FCSTD DOCUMENT  (FreeCAD 1.1R41365 (Git))
Label: FlexureAssembly
License: All rights reserved
LicenseURL: https://en.wikipedia.org/wiki/All_rights_reserved
objects: App::Link×7, App::Point×1, App::FeaturePython×1, Assembly::JointGroup×1, Assembly::AssemblyObject×1
EXTERNAL_REF file=WireMount.FCStd obj=Body
EXTERNAL_REF file=FlexureWire.FCStd obj=Body
EXTERNAL_REF file=FlexureStiffener.FCStd obj=Body
EXTERNAL_REF file=WireMountFixture.FCStd obj=Body

FEATURE [App::Point] Origin001
  Role = Origin
FEATURE [App::Link] WireMount  label="WireMount1"
  LinkedObject = -> <external WireMount.FCStd>#Body
FEATURE [App::FeaturePython] GroundedJoint  # Assembly grounded joint (typed FeaturePython)
  ObjectToGround = -> WireMount
FEATURE [Assembly::JointGroup] Joints
  Group = -> [GroundedJoint]
FEATURE [App::Link] WireMount001  label="WireMount2"
  LinkPlacement = pos=(0,-55,3) rot=(1,0,0;3.14159rad)
  LinkedObject = -> <external WireMount.FCStd>#Body
  Placement = pos=(0,-55,3) rot=(1,0,0;3.14159rad)
FEATURE [App::Link] FlexureWire  label="FlexureWire1"
  LinkPlacement = pos=(8,3.5,1.5) rot=(0,0,1;0rad)
  LinkedObject = -> <external FlexureWire.FCStd>#Body
  Placement = pos=(8,3.5,1.5) rot=(0,0,1;0rad)
FEATURE [App::Link] FlexureWire001  label="FlexureWire2"
  LinkPlacement = pos=(-8.00001,3.5,1.5) rot=(0,0,1;0rad)
  LinkedObject = -> <external FlexureWire.FCStd>#Body
  Placement = pos=(-8.00001,3.5,1.5) rot=(0,0,1;0rad)
FEATURE [App::Link] Rod  label="FlexureStiffener1"
  LinkPlacement = pos=(-8,-27.5,1.5) rot=(0,0,1;0rad)
  LinkedObject = -> <external FlexureStiffener.FCStd>#Body
  Placement = pos=(-8,-27.5,1.5) rot=(0,0,1;0rad)
FEATURE [App::Link] FlexureStiffener  label="FlexureStiffener2"
  LinkPlacement = pos=(8,-27.5,1.5) rot=(0,0,1;0rad)
  LinkedObject = -> <external FlexureStiffener.FCStd>#Body
  Placement = pos=(8,-27.5,1.5) rot=(0,0,1;0rad)
FEATURE [App::Link] WireMountFixture
  LinkPlacement = pos=(0,-27.5,-5) rot=(0,0,1;0rad)
  LinkedObject = -> <external WireMountFixture.FCStd>#Body
  Placement = pos=(0,-27.5,-5) rot=(0,0,1;0rad)
FEATURE [Assembly::AssemblyObject] Assembly  label="FlexureAssembly"
  Group = -> [Joints,WireMount,GroundedJoint,WireMount001,FlexureWire,FlexureWire001,Rod,FlexureStiffener,WireMountFixture]
  Origin = -> Origin
  Type = Assembly

RESOLVED EXTERNAL PARTS (link-assembly join: the EXTERNAL_REF files above that resolve inside this repo's crawl, each included once):
---- part FlexureStiffener.FCStd = doc fcstd_d9e3d32cc4ef ----
FCSTD DOCUMENT  (FreeCAD 1.1R41365 (Git))
Label: FlexureStiffener
License: All rights reserved
LicenseURL: https://en.wikipedia.org/wiki/All_rights_reserved
objects: App::Point×1, Sketcher::SketchObject×1, PartDesign::Pad×1, PartDesign::Fillet×1, PartDesign::Body×1
note: 9 computed .brp shape members not serialized (recipe doc carries the construction recipe); baked Part::Feature solids carry a one-line shape summary decoded from their .brp

FEATURE [App::Point] Origin001
  Role = Origin
FEATURE [Sketcher::SketchObject] Sketch
  ArcFitTolerance = 1e-06
  AttachmentSupport = -> [XZ_Plane]
  ExternalTypes = [0]
  FullyConstrained = true
  MakeInternals = false
  MapMode = 5
  Placement = pos=(0,0,0) rot=(1,0,0;1.5708rad)
  sketch-geometry (14):
    g0: LineSegment StartX=0.669696 StartY=1.61679 StartZ=0 EndX=-0.669696 EndY=1.61679 EndZ=0
    g1: LineSegment StartX=-0.669696 StartY=1.61679 StartZ=0 EndX=-1.61679 EndY=0.669696 EndZ=0
    g2: LineSegment StartX=-1.61679 StartY=0.669696 StartZ=0 EndX=-1.61679 EndY=-0.669696 EndZ=0
    g3: LineSegment StartX=-1.61679 StartY=-0.669696 StartZ=0 EndX=-0.669696 EndY=-1.61679 EndZ=0
    g4: LineSegment StartX=-0.669696 StartY=-1.61679 StartZ=0 EndX=0.669696 EndY=-1.61679 EndZ=0
    g5: LineSegment StartX=0.669696 StartY=-1.61679 StartZ=0 EndX=1.61679 EndY=-0.669696 EndZ=0
    g6: LineSegment StartX=1.61679 StartY=-0.669696 StartZ=0 EndX=1.61679 EndY=0.669696 EndZ=0
    g7: LineSegment StartX=1.61679 StartY=0.669696 StartZ=0 EndX=0.669696 EndY=1.61679 EndZ=0
    g8: Circle [constr] CenterX=0 CenterY=0 CenterZ=0 NormalX=0 NormalY=0 NormalZ=1 AngleXU=0 Radius=1.75
    g9: LineSegment StartX=-0.3 StartY=-0.325 StartZ=0 EndX=0.3 EndY=-0.325 EndZ=0
    g10: LineSegment StartX=0.3 StartY=-0.325 StartZ=0 EndX=0.3 EndY=0.325 EndZ=0
    g11: LineSegment StartX=0.3 StartY=0.325 StartZ=0 EndX=-0.3 EndY=0.325 EndZ=0
    g12: LineSegment StartX=-0.3 StartY=0.325 StartZ=0 EndX=-0.3 EndY=-0.325 EndZ=0
    g13: GeomPoint [constr] X=0 Y=0 Z=0
  constraints (32):
    c: Coincident(g0,g1)
    c: Coincident(g1,g2)
    c: Coincident(g2,g3)
    c: Coincident(g3,g4)
    c: Coincident(g4,g5)
    c: Coincident(g5,g6)
    c: Coincident(g6,g7)
    c: Coincident(g7,g0)
    c: Equal(g0, g1-g7) x7
    c: PointOnObject(g0,g8)
    c: PointOnObject(g1,g8)
    c: PointOnObject(g2,g8)
    c: PointOnObject(g3,g8)
    c: PointOnObject(g4,g8)
    c: PointOnObject(g5,g8)
    c: PointOnObject(g6,g8)
    c: PointOnObject(g7,g8)
    c: Coincident(g8,g-1)
    c: Vertical(g6)
    c: Diameter(g8) = 3.5
    c: Coincident(g9,g10)
    c: Coincident(g10,g11)
    c: Coincident(g11,g12)
    c: Coincident(g12,g9)
    c: Horizontal(g9)
    c: Horizontal(g11)
    c: Vertical(g10)
    c: Vertical(g12)
    c: Symmetric(g11,g9,g13)
    c: Coincident(g13,g8)
    c: DistanceY(g10,g10) = 0.65
    c: DistanceX(g11,g11) = 0.6
FEATURE [PartDesign::Pad] Pad
  Direction = (0,-1,2e-16)
  Length = 40
  Length2 = 10
  Midplane = true
  Placement = pos=(0,0,0) rot=(1,0,0;1.5708rad)
  Profile = -> Sketch
  ReferenceAxis = -> Sketch [N_Axis]
  Refine = true
  Suppressed = false
  Type = 0
FEATURE [PartDesign::Fillet] Fillet
  Base = -> Pad [Edge5,Edge8,Edge20,Edge17]
  BaseFeature = -> Pad
  Placement = pos=(0,0,0) rot=(1,0,0;1.5708rad)
  Radius = 0.25
  Refine = true
  SupportTransform = false
  Suppressed = false
  UseAllEdges = false
FEATURE [PartDesign::Body] Body  label="FlexureStiffener"
  AllowCompound = false
  Group = -> [Sketch,Pad,Fillet]
  Origin = -> Origin
  Tip = -> Fillet
---- part FlexureWire.FCStd = doc fcstd_ac3010708b95 ----
FCSTD DOCUMENT  (FreeCAD 1.1R41365 (Git))
Label: FlexureWire
License: All rights reserved
LicenseURL: https://en.wikipedia.org/wiki/All_rights_reserved
objects: App::Point×1, Sketcher::SketchObject×1, PartDesign::Pad×1, PartDesign::Body×1
note: 6 computed .brp shape members not serialized (recipe doc carries the construction recipe); baked Part::Feature solids carry a one-line shape summary decoded from their .brp

FEATURE [App::Point] Origin001
  Role = Origin
FEATURE [Sketcher::SketchObject] Sketch
  ArcFitTolerance = 1e-06
  AttachmentSupport = -> [XZ_Plane]
  ExternalTypes = [0]
  FullyConstrained = true
  MakeInternals = false
  MapMode = 5
  Placement = pos=(0,0,0) rot=(1,0,0;1.5708rad)
  sketch-geometry (1):
    g0: Circle CenterX=0 CenterY=0 CenterZ=0 NormalX=0 NormalY=0 NormalZ=1 AngleXU=0 Radius=0.25
  constraints (2):
    c: Coincident(g0,g-1)
    c: Diameter(g0) = 0.5
FEATURE [PartDesign::Pad] Pad
  Direction = (0,-1,0)
  Length = 62
  Length2 = 10
  Placement = pos=(0,0,0) rot=(1,0,0;1.5708rad)
  Profile = -> Sketch
  ReferenceAxis = -> Sketch [N_Axis]
  Refine = true
  Suppressed = false
  Type = 0
FEATURE [PartDesign::Body] Body  label="FlexureWire"
  AllowCompound = false
  Group = -> [Sketch,Pad]
  Origin = -> Origin
  Tip = -> Pad
---- part WireMount.FCStd = doc fcstd_70210a3bc8ae ----
FCSTD DOCUMENT  (FreeCAD 1.1R41365 (Git))
Label: WireMount
License: All rights reserved
LicenseURL: https://en.wikipedia.org/wiki/All_rights_reserved
objects: Sketcher::SketchObject×3, PartDesign::Pocket×2, PartDesign::Chamfer×2, App::Point×1, PartDesign::Pad×1, PartDesign::Fillet×1, PartDesign::Mirrored×1, PartDesign::Body×1
note: 27 computed .brp shape members not serialized (recipe doc carries the construction recipe); baked Part::Feature solids carry a one-line shape summary decoded from their .brp

FEATURE [App::Point] Origin001
  Role = Origin
FEATURE [Sketcher::SketchObject] Sketch
  ArcFitTolerance = 1e-06
  AttachmentSupport = -> [XY_Plane]
  ExternalTypes = [0]
  FullyConstrained = true
  MakeInternals = false
  MapMode = 5
  sketch-geometry (5):
    g0: LineSegment StartX=-10 StartY=-2.75 StartZ=0 EndX=0 EndY=-2.75 EndZ=0
    g1: LineSegment StartX=0 StartY=-2.75 StartZ=0 EndX=0 EndY=2.75 EndZ=0
    g2: LineSegment StartX=0 StartY=2.75 StartZ=0 EndX=-10 EndY=2.75 EndZ=0
    g3: LineSegment StartX=-10 StartY=2.75 StartZ=0 EndX=-10 EndY=-2.75 EndZ=0
    g4: GeomPoint [constr] X=0 Y=0 Z=0
  constraints (12):
    c: Coincident(g0,g1)
    c: Coincident(g1,g2)
    c: Coincident(g2,g3)
    c: Coincident(g3,g0)
    c: Horizontal(g0)
    c: Horizontal(g2)
    c: Vertical(g1)
    c: Vertical(g3)
    c: Coincident(g4,g-1)
    c: DistanceX(g0,g0) = 10
    c: DistanceY(g1,g1) = 5.5
    c: Symmetric(g1,g1,g4)
FEATURE [PartDesign::Pad] Pad
  Direction = (0,0,1)
  Length = 3
  Length2 = 10
  Profile = -> Sketch
  ReferenceAxis = -> Sketch [N_Axis]
  Refine = true
  Suppressed = false
  Type = 0
FEATURE [Sketcher::SketchObject] Sketch001
  ArcFitTolerance = 1e-06
  AttachmentSupport = -> [Pad]
  ExternalTypes = [0]
  FullyConstrained = true
  MakeInternals = false
  MapMode = 5
  Placement = pos=(0,0,3) rot=(0,0,1;0rad)
  sketch-geometry (1):
    g0: Circle CenterX=-6 CenterY=0 CenterZ=0 NormalX=0 NormalY=0 NormalZ=1 AngleXU=0 Radius=1.1
  constraints (3):
    c: Diameter(g0) = 2.2
    c: DistanceX(g0,g-1) = 6
    c: PointOnObject(g0,g-1)
FEATURE [PartDesign::Pocket] Pocket
  BaseFeature = -> Pad
  Direction = (0,0,-1)
  Length = 5
  Length2 = 5
  Profile = -> Sketch001
  ReferenceAxis = -> Sketch001 [N_Axis]
  Refine = true
  Suppressed = false
  Type = 1
FEATURE [Sketcher::SketchObject] Sketch002
  ArcFitTolerance = 1e-06
  AttachmentSupport = -> [Pocket]
  ExternalTypes = [0]
  FullyConstrained = true
  MakeInternals = false
  MapMode = 5
  Placement = pos=(0,-2.75,0) rot=(1,0,0;1.5708rad)
  sketch-geometry (5):
    g0: LineSegment StartX=-8.3 StartY=1.2 StartZ=0 EndX=-7.7 EndY=1.2 EndZ=0
    g1: LineSegment StartX=-7.7 StartY=1.2 StartZ=0 EndX=-7.7 EndY=1.8 EndZ=0
    g2: LineSegment StartX=-7.7 StartY=1.8 StartZ=0 EndX=-8.3 EndY=1.8 EndZ=0
    g3: LineSegment StartX=-8.3 StartY=1.8 StartZ=0 EndX=-8.3 EndY=1.2 EndZ=0
    g4: GeomPoint [constr] X=-8 Y=1.5 Z=0
  constraints (13):
    c: Coincident(g0,g1)
    c: Coincident(g1,g2)
    c: Coincident(g2,g3)
    c: Coincident(g3,g0)
    c: Horizontal(g0)
    c: Horizontal(g2)
    c: Vertical(g1)
    c: Vertical(g3)
    c: Symmetric(g2,g0,g4)
    c: DistanceY(g3,g3) = 0.6
    c: DistanceX(g0,g0) = 0.6
    c: DistanceY(g-1,g4) = 1.5
    c: DistanceX(g4,g-1) = 8
FEATURE [PartDesign::Pocket] Pocket001
  BaseFeature = -> Pocket
  Direction = (0,1,-2e-16)
  Length = 5
  Length2 = 5
  Profile = -> Sketch002
  ReferenceAxis = -> Sketch002 [N_Axis]
  Refine = true
  Suppressed = false
  Type = 1
FEATURE [PartDesign::Fillet] Fillet
  Base = -> Pocket001 [Edge1,Edge9]
  BaseFeature = -> Pocket001
  Radius = 0.75
  Refine = true
  SupportTransform = false
  Suppressed = false
  UseAllEdges = false
FEATURE [PartDesign::Mirrored] Mirrored
  BaseFeature = -> Fillet
  MirrorPlane = -> YZ_Plane
  Refine = true
  Suppressed = false
  TransformMode = 1
FEATURE [PartDesign::Chamfer] Chamfer
  Angle = 45
  Base = -> Mirrored [Edge50,Edge52]
  BaseFeature = -> Mirrored
  ChamferType = 0
  FlipDirection = false
  Refine = true
  Size = 1.2
  Size2 = 1
  SupportTransform = false
  Suppressed = false
  UseAllEdges = false
FEATURE [PartDesign::Chamfer] Chamfer001
  Angle = 45
  Base = -> Chamfer [Edge6]
  BaseFeature = -> Chamfer
  ChamferType = 0
  FlipDirection = false
  Refine = true
  Size = 0.4
  Size2 = 1
  SupportTransform = false
  Suppressed = false
  UseAllEdges = false
FEATURE [PartDesign::Body] Body  label="WireMount"
  AllowCompound = false
  Group = -> [Sketch,Pad,Sketch001,Pocket,Sketch002,Pocket001,Fillet,Mirrored,Chamfer,Chamfer001]
  Origin = -> Origin
  Tip = -> Chamfer001
---- part WireMountFixture.FCStd = doc fcstd_843f589c6978 ----
FCSTD DOCUMENT  (FreeCAD 1.1R41365 (Git))
Label: WireMountFixture
License: All rights reserved
LicenseURL: https://en.wikipedia.org/wiki/All_rights_reserved
objects: Sketcher::SketchObject×7, PartDesign::Pocket×6, PartDesign::Fillet×2, PartDesign::Chamfer×2, App::Point×1, PartDesign::Pad×1, Spreadsheet::Sheet×1, PartDesign::Mirrored×1, PartDesign::Body×1
note: 50 computed .brp shape members not serialized (recipe doc carries the construction recipe); baked Part::Feature solids carry a one-line shape summary decoded from their .brp

FEATURE [App::Point] Origin001
  Role = Origin
FEATURE [Sketcher::SketchObject] Sketch
  ArcFitTolerance = 1e-06
  AttachmentSupport = -> [XY_Plane]
  ExternalTypes = [0]
  FullyConstrained = true
  MakeInternals = false
  MapMode = 5
  sketch-geometry (5):
    g0: LineSegment StartX=-12.5 StartY=35 StartZ=0 EndX=-12.5 EndY=0 EndZ=0
    g1: LineSegment StartX=-12.5 StartY=0 StartZ=0 EndX=12.5 EndY=0 EndZ=0
    g2: LineSegment StartX=12.5 StartY=0 StartZ=0 EndX=12.5 EndY=35 EndZ=0
    g3: LineSegment StartX=12.5 StartY=35 StartZ=0 EndX=-12.5 EndY=35 EndZ=0
    g4: GeomPoint [constr] X=0 Y=0 Z=0
  constraints (12):
    c: Coincident(g0,g1)
    c: Coincident(g1,g2)
    c: Coincident(g2,g3)
    c: Coincident(g3,g0)
    c: Vertical(g0)
    c: Vertical(g2)
    c: Horizontal(g1)
    c: Horizontal(g3)
    c: Coincident(g4,g-1)
    c: DistanceX(g3,g3) = 25
    c: Symmetric(g1,g1,g4)
    c: DistanceY(g2,g2) = 35
FEATURE [PartDesign::Pad] Pad
  Direction = (0,0,1)
  Length = 6
  Length2 = 10
  Profile = -> Sketch
  ReferenceAxis = -> Sketch [N_Axis]
  Refine = true
  Suppressed = false
  Type = 0
FEATURE [Sketcher::SketchObject] Sketch002
  ArcFitTolerance = 1e-06
  AttachmentSupport = -> [Pad]
  ExternalTypes = [0]
  FullyConstrained = true
  MakeInternals = false
  MapMode = 5
  Placement = pos=(0,0,6) rot=(0,0,1;0rad)
  sketch-geometry (5):
    g0: LineSegment StartX=10.05 StartY=24.7 StartZ=0 EndX=-10.05 EndY=24.7 EndZ=0
    g1: LineSegment StartX=-10.05 StartY=24.7 StartZ=0 EndX=-10.05 EndY=30.3 EndZ=0
    g2: LineSegment StartX=-10.05 StartY=30.3 StartZ=0 EndX=10.05 EndY=30.3 EndZ=0
    g3: LineSegment StartX=10.05 StartY=30.3 StartZ=0 EndX=10.05 EndY=24.7 EndZ=0
    g4: GeomPoint [constr] X=0 Y=27.5 Z=0
  constraints (13):
    c: Coincident(g0,g1)
    c: Coincident(g1,g2)
    c: Coincident(g2,g3)
    c: Coincident(g3,g0)
    c: Horizontal(g0)
    c: Horizontal(g2)
    c: Vertical(g1)
    c: Vertical(g3)
    c: Symmetric(g2,g0,g4)
    c: PointOnObject(g4,g-2)
    c: DistanceY(g1,g1) = 5.6
    c: Distance(g0,g0) = 20.1
    c: DistanceY(g-1,g4) = 27.5
FEATURE [Spreadsheet::Sheet] Spreadsheet  label="Parameters"
  cells = A1='Cabel Length; B1(CableLength)==75 mm
FEATURE [PartDesign::Pocket] Pocket
  BaseFeature = -> Pad
  Direction = (0,0,-1)
  Length = 1.5
  Length2 = 5
  Profile = -> Sketch002
  ReferenceAxis = -> Sketch002 [N_Axis]
  Refine = true
  Suppressed = false
  Type = 0
FEATURE [Sketcher::SketchObject] Sketch004
  ArcFitTolerance = 1e-06
  AttachmentSupport = -> [Pocket]
  ExternalGeometry = -> [Pocket]
  ExternalTypes = [0,0,0,0]
  FullyConstrained = true
  MakeInternals = false
  MapMode = 5
  Placement = pos=(0,0,6) rot=(0,0,1;0rad)
  sketch-geometry (4):
    g0: Circle CenterX=-10.05 CenterY=30.3 CenterZ=0 NormalX=0 NormalY=0 NormalZ=1 AngleXU=0 Radius=1
    g1: Circle CenterX=10.05 CenterY=30.3 CenterZ=0 NormalX=0 NormalY=0 NormalZ=1 AngleXU=0 Radius=1
    g2: Circle CenterX=-10.05 CenterY=24.7 CenterZ=0 NormalX=0 NormalY=0 NormalZ=1 AngleXU=0 Radius=1
    g3: Circle CenterX=10.05 CenterY=24.7 CenterZ=0 NormalX=0 NormalY=0 NormalZ=1 AngleXU=0 Radius=1
  constraints (9):
    c: Equal(g1,g0)
    c: Diameter(g0) = 2
    c: Horizontal(g1,g0)
    c: Vertical(g-4,g1)
    c: Coincident(g0,g-3)
    c: Coincident(g2,g-6)
    c: Coincident(g3,g-5)
    c: Equal(g2,g0)
    c: Equal(g0,g3)
FEATURE [PartDesign::Pocket] Pocket002
  BaseFeature = -> Pocket
  Direction = (0,0,-1)
  Length = 2
  Length2 = 5
  Profile = -> Sketch004
  ReferenceAxis = -> Sketch004 [N_Axis]
  Refine = true
  Suppressed = false
  Type = 0
FEATURE [Sketcher::SketchObject] Sketch006
  ArcFitTolerance = 1e-06
  AttachmentSupport = -> [Pocket002]
  ExternalTypes = [0]
  FullyConstrained = true
  MakeInternals = false
  MapMode = 5
  Placement = pos=(0,0,6) rot=(0,0,1;0rad)
  sketch-geometry (1):
    g0: Circle CenterX=0 CenterY=27.5 CenterZ=0 NormalX=0 NormalY=0 NormalZ=1 AngleXU=0 Radius=1.5
  constraints (3):
    c: PointOnObject(g0,g-2)
    c: Diameter(g0) = 3
    c: DistanceY(g-1,g0) = 27.5
FEATURE [PartDesign::Fillet] Fillet001
  Base = -> Pocket002 [Edge25,Edge23,Edge29,Edge30,Edge42,Edge41,Edge35]
  BaseFeature = -> Pocket002
  Radius = 0.5
  Refine = true
  SupportTransform = false
  Suppressed = false
  UseAllEdges = false
FEATURE [PartDesign::Pocket] Pocket004
  BaseFeature = -> Fillet001
  Direction = (0,0,-1)
  Length = 5
  Length2 = 5
  Profile = -> Sketch006
  ReferenceAxis = -> Sketch006 [N_Axis]
  Refine = true
  Suppressed = false
  Type = 1
FEATURE [PartDesign::Mirrored] Mirrored
  BaseFeature = -> Pocket004
  MirrorPlane = -> XZ_Plane
  Refine = true
  Suppressed = false
  TransformMode = 1
FEATURE [Sketcher::SketchObject] Sketch005
  ArcFitTolerance = 1e-06
  AttachmentSupport = -> [Mirrored]
  ExternalTypes = [0]
  FullyConstrained = true
  MakeInternals = false
  MapMode = 5
  Placement = pos=(0,-1.4e-15,6) rot=(0,0,1;0rad)
  sketch-geometry (5):
    g0: ArcOfCircle CenterX=0 CenterY=11 CenterZ=0 NormalX=0 NormalY=0 NormalZ=1 AngleXU=0 Radius=7 StartAngle=2e-16 EndAngle=3.14159
    g1: ArcOfCircle CenterX=-4e-16 CenterY=-11 CenterZ=0 NormalX=0 NormalY=0 NormalZ=1 AngleXU=0 Radius=7 StartAngle=3.14159 EndAngle=6.28319
    g2: LineSegment StartX=7 StartY=11 StartZ=0 EndX=7 EndY=-11 EndZ=0
    g3: LineSegment StartX=-7 StartY=11 StartZ=0 EndX=-7 EndY=-11 EndZ=0
    g4: LineSegment [constr] StartX=-7 StartY=0 StartZ=0 EndX=0 EndY=0 EndZ=0
  constraints (12):
    c: Tangent(g0,g2) = 1.5708
    c: Tangent(g0,g3) = -1.5708
    c: Tangent(g1,g2) = 1.5708
    c: Tangent(g1,g3) = -1.5708
    c: Equal(g0,g1)
    c: Vertical(g3)
    c: PointOnObject(g0,g-2)
    c: Horizontal(g4)
    c: Coincident(g4,g-1)
    c: Radius(g0) = 7
    c: Symmetric(g3,g3,g4)
    c: DistanceY(g1,g0) = 22
FEATURE [PartDesign::Pocket] Pocket003
  BaseFeature = -> Mirrored
  Direction = (0,0,-1)
  Length = 9
  Length2 = 5
  Profile = -> Sketch005
  ReferenceAxis = -> Sketch005 [N_Axis]
  Refine = true
  Suppressed = false
  Type = 0
FEATURE [PartDesign::Chamfer] Chamfer002
  Angle = 45
  Base = -> Pocket003 [Edge36]
  BaseFeature = -> Pocket003
  ChamferType = 0
  FlipDirection = false
  Refine = true
  Size = 2
  Size2 = 1
  SupportTransform = false
  Suppressed = false
  UseAllEdges = false
FEATURE [Sketcher::SketchObject] Sketch008
  ArcFitTolerance = 1e-06
  AttachmentSupport = -> [Chamfer002]
  ExternalTypes = [0]
  FullyConstrained = true
  MakeInternals = false
  MapMode = 5
  Placement = pos=(0,-1.4e-15,6) rot=(0,0,1;0rad)
  sketch-geometry (5):
    g0: LineSegment StartX=-16 StartY=-21 StartZ=0 EndX=16 EndY=-21 EndZ=0
    g1: LineSegment StartX=16 StartY=-21 StartZ=0 EndX=16 EndY=20 EndZ=0
    g2: LineSegment StartX=16 StartY=20 StartZ=0 EndX=-16 EndY=20 EndZ=0
    g3: LineSegment StartX=-16 StartY=20 StartZ=0 EndX=-16 EndY=-21 EndZ=0
    g4: GeomPoint [constr] X=0 Y=-0.5 Z=0
  constraints (13):
    c: Coincident(g0,g1)
    c: Coincident(g1,g2)
    c: Coincident(g2,g3)
    c: Coincident(g3,g0)
    c: Horizontal(g0)
    c: Horizontal(g2)
    c: Vertical(g1)
    c: Vertical(g3)
    c: Symmetric(g2,g0,g4)
    c: PointOnObject(g4,g-2)
    c: Distance(g-1,g2) = 20
    c: Distance(g0,g0) = 32
    c: Distance(g-1,g0) = 21
FEATURE [PartDesign::Pocket] Pocket005
  BaseFeature = -> Chamfer002
  Direction = (0,0,-1)
  Length = 2.5
  Length2 = 5
  Profile = -> Sketch008
  ReferenceAxis = -> Sketch008 [N_Axis]
  Refine = true
  Suppressed = false
  Type = 0
FEATURE [PartDesign::Chamfer] Chamfer
  Angle = 45
  Base = -> Pocket005 [Edge26,Edge32]
  BaseFeature = -> Pocket005
  ChamferType = 0
  FlipDirection = false
  Refine = true
  Size = 3
  Size2 = 1
  SupportTransform = false
  Suppressed = false
  UseAllEdges = false
FEATURE [Sketcher::SketchObject] Sketch009
  ArcFitTolerance = 1e-06
  AttachmentSupport = -> [Chamfer]
  ExternalTypes = [0]
  FullyConstrained = true
  MakeInternals = false
  MapMode = 5
  Placement = pos=(0,-35,-1.54e-14) rot=(1,0,0;1.5708rad)
  sketch-geometry (5):
    g0: LineSegment StartX=-9.5 StartY=2.5 StartZ=0 EndX=-9.5 EndY=1.5 EndZ=0
    g1: LineSegment StartX=-9.5 StartY=1.5 StartZ=0 EndX=-8.5 EndY=1.5 EndZ=0
    g2: LineSegment StartX=-8.5 StartY=1.5 StartZ=0 EndX=-8.5 EndY=2.5 EndZ=0
    g3: LineSegment StartX=-8.5 StartY=2.5 StartZ=0 EndX=-9.5 EndY=2.5 EndZ=0
    g4: GeomPoint [constr] X=-9 Y=2 Z=0
  constraints (13):
    c: Coincident(g0,g1)
    c: Coincident(g1,g2)
    c: Coincident(g2,g3)
    c: Coincident(g3,g0)
    c: Vertical(g0)
    c: Vertical(g2)
    c: Horizontal(g1)
    c: Horizontal(g3)
    c: Symmetric(g2,g0,g4)
    c: DistanceX(g3,g3) = 1
    c: Distance(g2,g2) = 1
    c: DistanceX(g4,g-1) = 9
    c: DistanceY(g-1,g4) = 2
FEATURE [PartDesign::Pocket] Pocket006
  BaseFeature = -> Chamfer
  Direction = (0,1,-2e-16)
  Length = 62
  Length2 = 5
  Profile = -> Sketch009
  ReferenceAxis = -> Sketch009 [N_Axis]
  Refine = true
  Suppressed = false
  Type = 0
FEATURE [PartDesign::Fillet] Fillet
  Base = -> Pocket006 [Edge25,Edge33,Edge37,Edge39,Edge43,Edge30,Edge29,Edge26,Edge35,Edge41]
  BaseFeature = -> Pocket006
  Radius = 1
  Refine = true
  SupportTransform = false
  Suppressed = false
  UseAllEdges = false
FEATURE [PartDesign::Body] Body  label="WireMountFixture"
  AllowCompound = false
  Group = -> [Sketch,Pad,Sketch002,Pocket,Sketch004,Pocket002,Sketch006,Fillet001,Pocket004,Mirrored,Sketch005,Pocket003,Chamfer002,Sketch008,Pocket005,Chamfer,Sketch009,Pocket006,Fillet]
  Origin = -> Origin
  Tip = -> Fillet
